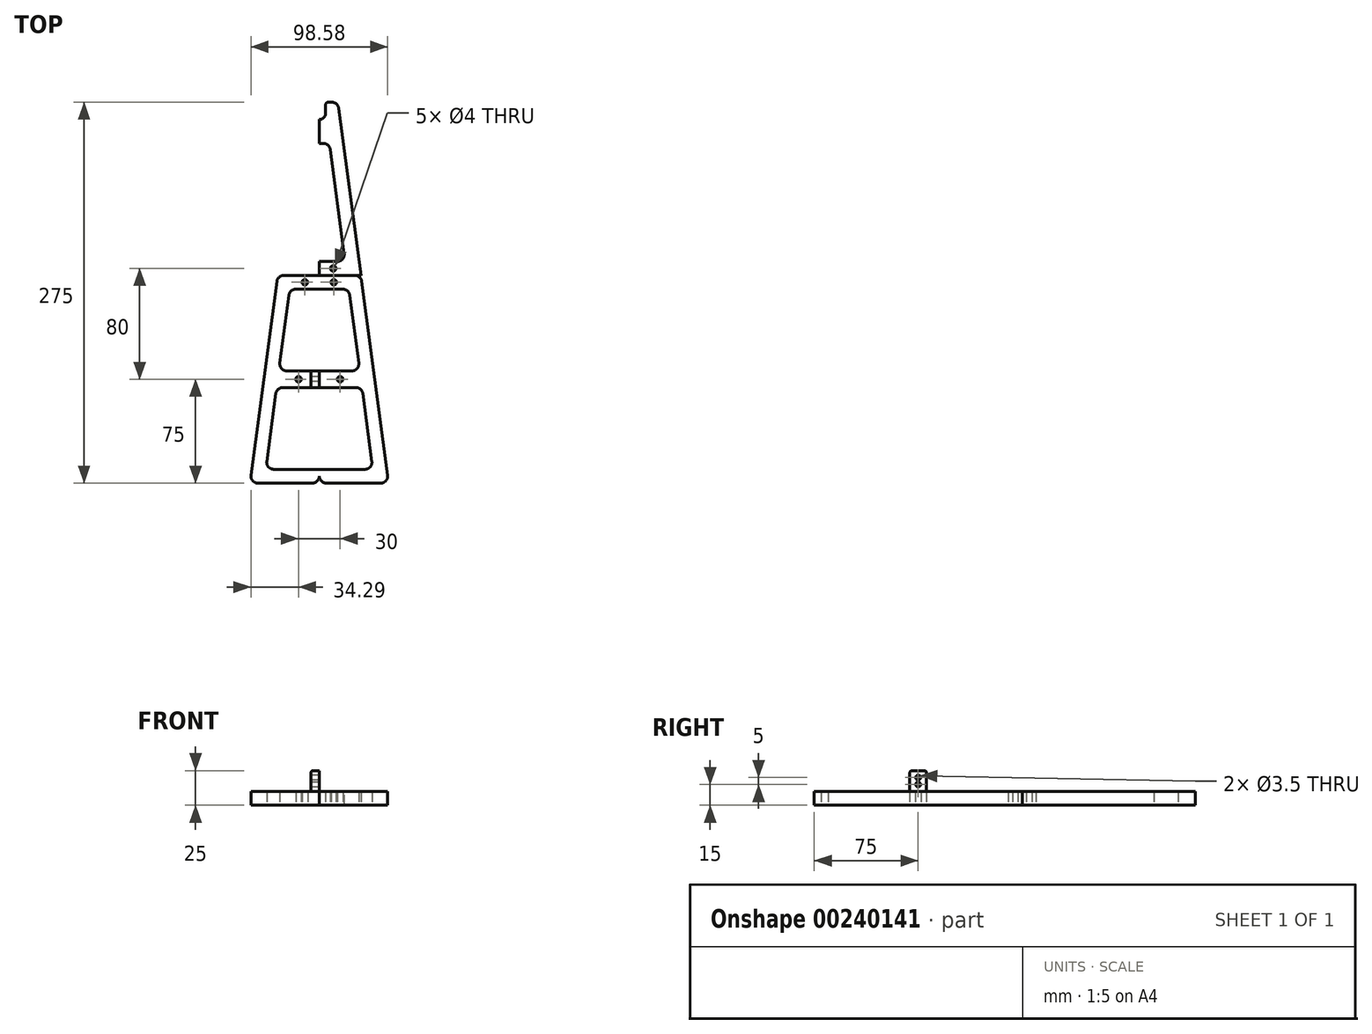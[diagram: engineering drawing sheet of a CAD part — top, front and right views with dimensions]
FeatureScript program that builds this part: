
annotation { "Feature Type Name" : "Feature", "Feature Type Description" : "" }
export const myFeature = defineFeature(function(context is Context, id is Id, definition is map)
    precondition{}
    {
        {
            var Q0;
            Q0=qCreatedBy(makeId("Top.planeOp"),FACE);
            var sketch = newSketch(context, id + "F0", { "sketchPlane" : qUnion([Q0])});
            skLineSegment(sketch, "E0.top", {"start": v(0, 75) * mm, "end": v(-30, 75) * mm});
            skPoint(sketch, "E0.middle", {"position": v(0, 0) * mm});
            skLineSegment(sketch, "E1", {"start": v(-30, 75) * mm, "end": v(-50, -75) * mm});
            skPoint(sketch, "E0.right.end.orphan", {"position": v(-50, 75) * mm});
            skPoint(sketch, "E0.left.end.orphan", {"position": v(50, 75) * mm});
            skLineSegment(sketch, "E2", {"start": v(0, 0) * mm, "end": v(0, 6) * mm});
            skLineSegment(sketch, "E3", {"start": v(-50, -75) * mm, "end": v(-40, -75) * mm});
            skLineSegment(sketch, "E4", {"start": v(-30, 75) * mm, "end": v(-20, 75) * mm});
            skLineSegment(sketch, "E5", {"start": v(0, 75) * mm, "end": v(0, 65) * mm});
            skLineSegment(sketch, "E6", {"start": v(0, 65) * mm, "end": v(-21.33, 65) * mm});
            skLineSegment(sketch, "E7", {"start": v(0, -75) * mm, "end": v(0, -65) * mm});
            skLineSegment(sketch, "E8", {"start": v(0, -65) * mm, "end": v(-38.67, -65) * mm});
            skLineSegment(sketch, "E9", {"start": v(0, 6) * mm, "end": v(-29.2, 6) * mm});
            skLineSegment(sketch, "E10", {"start": v(0, 0) * mm, "end": v(0, -6) * mm});
            skLineSegment(sketch, "E11", {"start": v(0, -6) * mm, "end": v(-30.8, -6) * mm});
            skLineSegment(sketch, "E12.trimOffspring", {"start": v(-30.8, -6) * mm, "end": v(-38.67, -65) * mm});
            skLineSegment(sketch, "E13", {"start": v(-21.33, 65) * mm, "end": v(-29.2, 6) * mm});
            skLineSegment(sketch, "E14.trimOffspring", {"start": v(0, -75) * mm, "end": v(-50, -75) * mm});
            skPoint(sketch, "E0.bottom.start.orphan", {"position": v(50, -75) * mm});
            skCircle(sketch, "E15", {"center": v(-15, 0) * mm, "radius": 2 * mm});
            skLineSegment(sketch, "E16", {"start": v(0, 65) * mm, "end": v(0, 70) * mm});
            skCircle(sketch, "E17", {"center": v(-10.41, 70) * mm, "radius": 2 * mm});
            skSolve(sketch);
        }
        {
            var Q0;
            Q0=qSketchRegion(id+"F0",true);
            extrude(context, id + "F1", {"entities" : qUnion([Q0]), "depth" : 10 * mm});
        }
        {
            var Q0;
            Q0=makeQuery(id+"F1.opExtrude","SWEPT_EDGE",EDGE,{"disambiguationData":[OSD([sQuery(id+"F0.wireOp",EDGE,"E6"),sQuery(id+"F0.wireOp",EDGE,"E13")])]});
            var Q1;
            Q1=makeQuery(id+"F1.opExtrude","SWEPT_EDGE",EDGE,{"disambiguationData":[OSD([sQuery(id+"F0.wireOp",EDGE,"E11"),sQuery(id+"F0.wireOp",EDGE,"E12.trimOffspring")])]});
            var Q2;
            Q2=makeQuery(id+"F1.opExtrude","SWEPT_EDGE",EDGE,{"disambiguationData":[OSD([sQuery(id+"F0.wireOp",EDGE,"E9"),sQuery(id+"F0.wireOp",EDGE,"E13")])]});
            var Q3;
            Q3=makeQuery(id+"F1.opExtrude","SWEPT_EDGE",EDGE,{"disambiguationData":[OSD([sQuery(id+"F0.wireOp",EDGE,"E8"),sQuery(id+"F0.wireOp",EDGE,"E12.trimOffspring")])]});
            var Q4;
            Q4=makeQuery(id+"F1.opExtrude","SWEPT_EDGE",EDGE,{"disambiguationData":[OSD([sQuery(id+"F0.wireOp",EDGE,"E1"),sQuery(id+"F0.wireOp",EDGE,"E14.trimOffspring")])]});
            fillet(context, id + "F2", {"entities" : qUnion([Q0, Q1, Q2, Q3, Q4]), "radius" : 5 * mm, "tangentPropagation" : true, "allowEdgeOverflow" : false});
        }
        {
            var Q0;
            Q0=makeQuery(id+"F1.opExtrude","SWEPT_BODY",BODY,{"disambiguationData":[OSD([sQuery(id+"F0.wireOp",EDGE,"E0.top"),sQuery(id+"F0.wireOp",EDGE,"E1"),sQuery(id+"F0.wireOp",EDGE,"E2"),sQuery(id+"F0.wireOp",EDGE,"E4"),sQuery(id+"F0.wireOp",EDGE,"E5"),sQuery(id+"F0.wireOp",EDGE,"E6"),sQuery(id+"F0.wireOp",EDGE,"E7"),sQuery(id+"F0.wireOp",EDGE,"E8"),sQuery(id+"F0.wireOp",EDGE,"E9"),sQuery(id+"F0.wireOp",EDGE,"E10"),sQuery(id+"F0.wireOp",EDGE,"E11"),sQuery(id+"F0.wireOp",EDGE,"E12.trimOffspring"),sQuery(id+"F0.wireOp",EDGE,"E13"),sQuery(id+"F0.wireOp",EDGE,"E14.trimOffspring"),sQuery(id+"F0.wireOp",EDGE,"E15"),sQuery(id+"F0.wireOp",EDGE,"E16"),sQuery(id+"F0.wireOp",EDGE,"E17")])]});
            var Q1;
            Q1=qCreatedBy(makeId("Right.planeOp"),FACE);
            mirror(context, id + "F3", {"operationType" : NewBodyOperationType.ADD, "entities" : qUnion([Q0]), "mirrorPlane" : qUnion([Q1])});
        }
        {
            var Q0;
            Q0=qCreatedBy(makeId("Top.planeOp"),FACE);
            var sketch = newSketch(context, id + "F4", { "sketchPlane" : qUnion([Q0])});
            skLineSegment(sketch, "E18", {"start": v(0, 0) * mm, "end": v(40, 0) * mm});
            skLineSegment(sketch, "E19", {"start": v(0, 75) * mm, "end": v(30, 75) * mm});
            skLineSegment(sketch, "E20", {"start": v(0, 75) * mm, "end": v(0, 85) * mm});
            skLineSegment(sketch, "E21", {"start": v(4.5, 200) * mm, "end": v(13.33, 200) * mm});
            skLineSegment(sketch, "E22", {"start": v(30, 75) * mm, "end": v(13.33, 200) * mm});
            skArc(sketch, "E23", {"start": v(0, 187.5) * mm, "mid": v(3.18, 188.82) * mm, "end": v(4.5, 192) * mm});
            skLineSegment(sketch, "E24", {"start": v(4.5, 200) * mm, "end": v(4.5, 192) * mm});
            skLineSegment(sketch, "E25", {"start": v(0, 75) * mm, "end": v(0, 80) * mm});
            skCircle(sketch, "E26", {"center": v(10, 80) * mm, "radius": 2 * mm});
            skLineSegment(sketch, "E27", {"start": v(0, 75) * mm, "end": v(10, 75) * mm});
            skLineSegment(sketch, "E28", {"start": v(10, 85) * mm, "end": v(18.67, 85) * mm});
            skLineSegment(sketch, "E29", {"start": v(18.67, 85) * mm, "end": v(10, 150) * mm});
            skLineSegment(sketch, "E30", {"start": v(10, 85) * mm, "end": v(0, 85) * mm});
            skLineSegment(sketch, "E31", {"start": v(18.67, 85) * mm, "end": v(7.31, 170.17) * mm});
            skLineSegment(sketch, "E32", {"start": v(7.31, 170.17) * mm, "end": v(0, 170.17) * mm});
            skLineSegment(sketch, "E33.trimOffspring", {"start": v(0, 170.17) * mm, "end": v(0, 187.5) * mm});
            skSolve(sketch);
        }
        {
            var Q0;
            Q0=qSketchRegion(id+"F4",true);
            extrude(context, id + "F5", {"entities" : qUnion([Q0]), "depth" : 10 * mm});
        }
        {
            var Q0;
            Q0=makeQuery(id+"F5.opExtrude","SWEPT_BODY",BODY,{"disambiguationData":[OSD([sQuery(id+"F4.wireOp",EDGE,"E19"),sQuery(id+"F4.wireOp",EDGE,"E20"),sQuery(id+"F4.wireOp",EDGE,"E21"),sQuery(id+"F4.wireOp",EDGE,"E22"),sQuery(id+"F4.wireOp",EDGE,"E23"),sQuery(id+"F4.wireOp",EDGE,"E24"),sQuery(id+"F4.wireOp",EDGE,"E25"),sQuery(id+"F4.wireOp",EDGE,"E26"),sQuery(id+"F4.wireOp",EDGE,"E27"),sQuery(id+"F4.wireOp",EDGE,"E28"),sQuery(id+"F4.wireOp",EDGE,"E30"),sQuery(id+"F4.wireOp",EDGE,"E31"),sQuery(id+"F4.wireOp",EDGE,"E32"),sQuery(id+"F4.wireOp",EDGE,"E33.trimOffspring")])]});
            var Q1;
            Q1=qCreatedBy(makeId("Right.planeOp"),FACE);
            mirror(context, id + "F6", {"entities" : qUnion([Q0]), "mirrorPlane" : qUnion([Q1])});
        }
        {
            var Q0;
            Q0=makeQuery(id+"F6.opPattern","COPY",EDGE,{"derivedFrom":makeQuery(id+"F5.opExtrude","SWEPT_EDGE",EDGE,{"disambiguationData":[OSD([sQuery(id+"F4.wireOp",EDGE,"E31"),sQuery(id+"F4.wireOp",EDGE,"E32")])]}),"instanceName":"1"});
            var Q1;
            Q1=makeQuery(id+"F5.opExtrude","SWEPT_EDGE",EDGE,{"disambiguationData":[OSD([sQuery(id+"F4.wireOp",EDGE,"E31"),sQuery(id+"F4.wireOp",EDGE,"E32")])]});
            var Q2;
            Q2=makeQuery(id+"F6.opPattern","COPY",EDGE,{"derivedFrom":makeQuery(id+"F5.opExtrude","SWEPT_EDGE",EDGE,{"disambiguationData":[OSD([sQuery(id+"F4.wireOp",EDGE,"E28"),sQuery(id+"F4.wireOp",EDGE,"E31")])]}),"instanceName":"1"});
            var Q3;
            Q3=makeQuery(id+"F5.opExtrude","SWEPT_EDGE",EDGE,{"disambiguationData":[OSD([sQuery(id+"F4.wireOp",EDGE,"E28"),sQuery(id+"F4.wireOp",EDGE,"E31")])]});
            var Q4;
            Q4=makeQuery(id+"F6.opPattern","COPY",EDGE,{"derivedFrom":makeQuery(id+"F5.opExtrude","SWEPT_EDGE",EDGE,{"disambiguationData":[OSD([sQuery(id+"F4.wireOp",EDGE,"E21"),sQuery(id+"F4.wireOp",EDGE,"E22")])]}),"instanceName":"1"});
            var Q5;
            Q5=makeQuery(id+"F5.opExtrude","SWEPT_EDGE",EDGE,{"disambiguationData":[OSD([sQuery(id+"F4.wireOp",EDGE,"E21"),sQuery(id+"F4.wireOp",EDGE,"E22")])]});
            fillet(context, id + "F7", {"entities" : qUnion([Q0, Q1, Q2, Q3, Q4, Q5]), "radius" : 5 * mm, "tangentPropagation" : true, "allowEdgeOverflow" : false});
        }
        {
            var Q0;
            Q0=makeQuery(id+"F5.opExtrude","SWEPT_EDGE",EDGE,{"disambiguationData":[OSD([sQuery(id+"F4.wireOp",EDGE,"E21"),sQuery(id+"F4.wireOp",EDGE,"E24")])]});
            var Q1;
            Q1=makeQuery(id+"F6.opPattern","COPY",EDGE,{"derivedFrom":makeQuery(id+"F5.opExtrude","SWEPT_EDGE",EDGE,{"disambiguationData":[OSD([sQuery(id+"F4.wireOp",EDGE,"E21"),sQuery(id+"F4.wireOp",EDGE,"E24")])]}),"instanceName":"1"});
            fillet(context, id + "F8", {"entities" : qUnion([Q0, Q1]), "radius" : 2 * mm, "tangentPropagation" : true, "allowEdgeOverflow" : false});
        }
        {
            var Q0;
            Q0=qCreatedBy(makeId("Top.planeOp"),FACE);
            var sketch = newSketch(context, id + "F9", { "sketchPlane" : qUnion([Q0])});
            skLineSegment(sketch, "E34", {"start": v(0, 0) * mm, "end": v(0, 6) * mm});
            skLineSegment(sketch, "E35", {"start": v(0, 6) * mm, "end": v(-6, 6) * mm});
            skLineSegment(sketch, "E36", {"start": v(-6, 6) * mm, "end": v(-6, -6) * mm});
            skLineSegment(sketch, "E37", {"start": v(-6, -6) * mm, "end": v(0, -6) * mm});
            skLineSegment(sketch, "E38", {"start": v(0, -6) * mm, "end": v(0, 0) * mm});
            skSolve(sketch);
        }
        {
            var Q0;
            Q0=qSketchRegion(id+"F9",true);
            extrude(context, id + "F10", {"entities" : qUnion([Q0]), "operationType" : NewBodyOperationType.ADD, "depth" : 25 * mm});
        }
        {
            var Q0;
            Q0=makeQuery(id+"F10.opExtrude","SWEPT_EDGE",EDGE,{"disambiguationData":[OSD([sQuery(id+"F9.wireOp",EDGE,"E36"),sQuery(id+"F9.wireOp",EDGE,"E37")])]});
            var Q1;
            Q1=makeQuery(id+"F10.opExtrude","CAP_EDGE",EDGE,{"disambiguationData":[OSD([sQuery(id+"F9.wireOp",EDGE,"E36")])],"isStart":false});
            var Q2;
            Q2=makeQuery(id+"F10.opExtrude","CAP_EDGE",EDGE,{"disambiguationData":[OSD([sQuery(id+"F9.wireOp",EDGE,"E37")])],"isStart":false});
            var Q3;
            Q3=makeQuery(id+"F10.opExtrude","SWEPT_EDGE",EDGE,{"disambiguationData":[OSD([sQuery(id+"F9.wireOp",EDGE,"E35"),sQuery(id+"F9.wireOp",EDGE,"E36")])]});
            var Q4;
            Q4=makeQuery(id+"F10.opExtrude","CAP_EDGE",EDGE,{"disambiguationData":[OSD([sQuery(id+"F9.wireOp",EDGE,"E35")])],"isStart":false});
            fillet(context, id + "F11", {"entities" : qUnion([Q0, Q1, Q2, Q3, Q4]), "radius" : 1.5 * mm, "tangentPropagation" : true, "allowEdgeOverflow" : false});
        }
        {
            var Q0;
            Q0=qCreatedBy(makeId("Right.planeOp"),FACE);
            var sketch = newSketch(context, id + "F12", { "sketchPlane" : qUnion([Q0])});
            skCircle(sketch, "E39", {"center": v(0, 20) * mm, "radius": 1.75 * mm});
            skCircle(sketch, "E40", {"center": v(0, 15) * mm, "radius": 1.75 * mm});
            skSolve(sketch);
        }
        {
            var Q0;
            Q0=qSketchRegion(id+"F12",true);
            extrude(context, id + "F13", {"entities" : qUnion([Q0]), "endBound" : BoundingType.SYMMETRIC, "depth" : 25 * mm});
        }
        {
            var Q0;
            Q0=makeQuery(id+"F13.opExtrude","SWEPT_BODY",BODY,{"disambiguationData":[OSD([sQuery(id+"F12.wireOp",EDGE,"E40")])]});
            var Q1;
            Q1=makeQuery(id+"F13.opExtrude","SWEPT_BODY",BODY,{"disambiguationData":[OSD([sQuery(id+"F12.wireOp",EDGE,"E39")])]});
            var Q2;
            Q2=makeQuery(id+"F1.opExtrude","SWEPT_BODY",BODY,{"disambiguationData":[OSD([sQuery(id+"F0.wireOp",EDGE,"E0.top"),sQuery(id+"F0.wireOp",EDGE,"E1"),sQuery(id+"F0.wireOp",EDGE,"E2"),sQuery(id+"F0.wireOp",EDGE,"E4"),sQuery(id+"F0.wireOp",EDGE,"E5"),sQuery(id+"F0.wireOp",EDGE,"E6"),sQuery(id+"F0.wireOp",EDGE,"E7"),sQuery(id+"F0.wireOp",EDGE,"E8"),sQuery(id+"F0.wireOp",EDGE,"E9"),sQuery(id+"F0.wireOp",EDGE,"E10"),sQuery(id+"F0.wireOp",EDGE,"E11"),sQuery(id+"F0.wireOp",EDGE,"E12.trimOffspring"),sQuery(id+"F0.wireOp",EDGE,"E13"),sQuery(id+"F0.wireOp",EDGE,"E14.trimOffspring"),sQuery(id+"F0.wireOp",EDGE,"E15"),sQuery(id+"F0.wireOp",EDGE,"E16"),sQuery(id+"F0.wireOp",EDGE,"E17")])]});
            booleanBodies(context, id + "F14", {"operationType" : BooleanOperationType.SUBTRACTION, "tools" : qUnion([Q0, Q1]), "targets" : qUnion([Q2])});
        }
        {
            var Q0;
            Q0=qCreatedBy(makeId("Top.planeOp"),FACE);
            var sketch = newSketch(context, id + "F15", { "sketchPlane" : qUnion([Q0])});
            skLineSegment(sketch, "E41.bottom", {"start": v(15, 65) * mm, "end": v(-15, 65) * mm});
            skLineSegment(sketch, "E41.top", {"start": v(15, 85) * mm, "end": v(-15, 85) * mm});
            skLineSegment(sketch, "E41.left", {"start": v(15, 65) * mm, "end": v(15, 85) * mm});
            skLineSegment(sketch, "E41.right", {"start": v(-15, 65) * mm, "end": v(-15, 85) * mm});
            skPoint(sketch, "E41.middle", {"position": v(0, 75) * mm});
            skLineSegment(sketch, "E42", {"start": v(0, 75) * mm, "end": v(0, 85) * mm});
            skLineSegment(sketch, "E43", {"start": v(0, 85) * mm, "end": v(0, 65) * mm});
            skLineSegment(sketch, "E44", {"start": v(0, 65) * mm, "end": v(-6, 65) * mm});
            skLineSegment(sketch, "E45", {"start": v(-6, 65) * mm, "end": v(-6, 85) * mm});
            skLineSegment(sketch, "E46", {"start": v(-6, 85) * mm, "end": v(0, 85) * mm});
            skSolve(sketch);
        }
        {
            var Q0;
            Q0=qSketchRegion(id+"F15",true);
            extrude(context, id + "F16", {"entities" : qUnion([Q0]), "depth" : 10 * mm});
        }
        {
            var Q0;
            Q0=qCreatedBy(makeId("Top.planeOp"),FACE);
            var sketch = newSketch(context, id + "F17", { "sketchPlane" : qUnion([Q0])});
            skLineSegment(sketch, "E47", {"start": v(0, 65) * mm, "end": v(0, 85) * mm});
            skLineSegment(sketch, "E48", {"start": v(0, 85) * mm, "end": v(-6, 85) * mm});
            skLineSegment(sketch, "E49", {"start": v(-6, 85) * mm, "end": v(-6, 65) * mm});
            skLineSegment(sketch, "E50", {"start": v(-6, 65) * mm, "end": v(0, 65) * mm});
            skSolve(sketch);
        }
        {
            var Q0;
            Q0=qSketchRegion(id+"F17",true);
            extrude(context, id + "F18", {"entities" : qUnion([Q0]), "depth" : 25 * mm});
        }
        {
            var Q0;
            Q0=makeQuery(id+"F16.opExtrude","SWEPT_BODY",BODY,{"disambiguationData":[OSD([sQuery(id+"F15.wireOp",EDGE,"E41.bottom"),sQuery(id+"F15.wireOp",EDGE,"E41.top"),sQuery(id+"F15.wireOp",EDGE,"E41.left"),sQuery(id+"F15.wireOp",EDGE,"E41.right"),sQuery(id+"F15.wireOp",EDGE,"E44"),sQuery(id+"F15.wireOp",EDGE,"E46")])]});
            var Q1;
            Q1=makeQuery(id+"F18.opExtrude","SWEPT_BODY",BODY,{"disambiguationData":[OSD([sQuery(id+"F17.wireOp",EDGE,"E47"),sQuery(id+"F17.wireOp",EDGE,"E48"),sQuery(id+"F17.wireOp",EDGE,"E49"),sQuery(id+"F17.wireOp",EDGE,"E50")])]});
            booleanBodies(context, id + "F19", {"operationType" : BooleanOperationType.UNION, "tools" : qUnion([Q0, Q1])});
        }
        {
            var Q0;
            Q0=makeQuery(id+"F16.opExtrude","SWEPT_BODY",BODY,{"disambiguationData":[OSD([sQuery(id+"F15.wireOp",EDGE,"E41.bottom"),sQuery(id+"F15.wireOp",EDGE,"E41.top"),sQuery(id+"F15.wireOp",EDGE,"E41.left"),sQuery(id+"F15.wireOp",EDGE,"E41.right"),sQuery(id+"F15.wireOp",EDGE,"E44"),sQuery(id+"F15.wireOp",EDGE,"E46")])]});
            transform(context, id + "F20", {"entities" : qUnion([Q0]), "transformType" : TransformType.TRANSLATION_3D, "dx" : 0 * mm, "dy" : 0 * mm, "dz" : 10 * mm, "makeCopy" : false});
        }
        {
            var Q0;
            Q0=qCreatedBy(makeId("Top.planeOp"),FACE);
            var sketch = newSketch(context, id + "F21", { "sketchPlane" : qUnion([Q0])});
            skCircle(sketch, "E51", {"center": v(-10, 80) * mm, "radius": 2 * mm});
            skCircle(sketch, "E52", {"center": v(10, 80) * mm, "radius": 2 * mm});
            skCircle(sketch, "E53", {"center": v(-10.4, 70) * mm, "radius": 2 * mm});
            skCircle(sketch, "E54", {"center": v(10.4, 70) * mm, "radius": 2 * mm});
            skSolve(sketch);
        }
        {
            var Q0;
            Q0=qSketchRegion(id+"F21",true);
            extrude(context, id + "F22", {"entities" : qUnion([Q0]), "depth" : 30 * mm});
        }
        {
            var Q0;
            Q0=makeQuery(id+"F22.opExtrude","SWEPT_BODY",BODY,{"disambiguationData":[OSD([sQuery(id+"F21.wireOp",EDGE,"E54")])]});
            var Q1;
            Q1=makeQuery(id+"F22.opExtrude","SWEPT_BODY",BODY,{"disambiguationData":[OSD([sQuery(id+"F21.wireOp",EDGE,"E53")])]});
            var Q2;
            Q2=makeQuery(id+"F22.opExtrude","SWEPT_BODY",BODY,{"disambiguationData":[OSD([sQuery(id+"F21.wireOp",EDGE,"E52")])]});
            var Q3;
            Q3=makeQuery(id+"F22.opExtrude","SWEPT_BODY",BODY,{"disambiguationData":[OSD([sQuery(id+"F21.wireOp",EDGE,"E51")])]});
            var Q4;
            Q4=makeQuery(id+"F16.opExtrude","SWEPT_BODY",BODY,{"disambiguationData":[OSD([sQuery(id+"F15.wireOp",EDGE,"E41.bottom"),sQuery(id+"F15.wireOp",EDGE,"E41.top"),sQuery(id+"F15.wireOp",EDGE,"E41.left"),sQuery(id+"F15.wireOp",EDGE,"E41.right"),sQuery(id+"F15.wireOp",EDGE,"E44"),sQuery(id+"F15.wireOp",EDGE,"E46")])]});
            booleanBodies(context, id + "F23", {"operationType" : BooleanOperationType.SUBTRACTION, "tools" : qUnion([Q0, Q1, Q2, Q3]), "targets" : qUnion([Q4])});
        }
        {
            var Q0;
            Q0=qCreatedBy(makeId("Right.planeOp"),FACE);
            var sketch = newSketch(context, id + "F24", { "sketchPlane" : qUnion([Q0])});
            skCircle(sketch, "E55", {"center": v(80, 27.23) * mm, "radius": 2 * mm});
            skCircle(sketch, "E56", {"center": v(70, 27.23) * mm, "radius": 2 * mm});
            skSolve(sketch);
        }
        {
            var Q0;
            Q0=qSketchRegion(id+"F24",true);
            extrude(context, id + "F25", {"entities" : qUnion([Q0]), "endBound" : BoundingType.SYMMETRIC, "depth" : 25 * mm});
        }
        {
            var Q0;
            Q0=makeQuery(id+"F25.opExtrude","SWEPT_BODY",BODY,{"disambiguationData":[OSD([sQuery(id+"F24.wireOp",EDGE,"E56")])]});
            var Q1;
            Q1=makeQuery(id+"F25.opExtrude","SWEPT_BODY",BODY,{"disambiguationData":[OSD([sQuery(id+"F24.wireOp",EDGE,"E55")])]});
            var Q2;
            Q2=makeQuery(id+"F16.opExtrude","SWEPT_BODY",BODY,{"disambiguationData":[OSD([sQuery(id+"F15.wireOp",EDGE,"E41.bottom"),sQuery(id+"F15.wireOp",EDGE,"E41.top"),sQuery(id+"F15.wireOp",EDGE,"E41.left"),sQuery(id+"F15.wireOp",EDGE,"E41.right"),sQuery(id+"F15.wireOp",EDGE,"E44"),sQuery(id+"F15.wireOp",EDGE,"E46")])]});
            booleanBodies(context, id + "F26", {"operationType" : BooleanOperationType.SUBTRACTION, "tools" : qUnion([Q0, Q1]), "targets" : qUnion([Q2])});
        }
        {
            var Q0;
            Q0=makeQuery(id+"F18.opExtrude","SWEPT_EDGE",EDGE,{"disambiguationData":[OSD([sQuery(id+"F17.wireOp",EDGE,"E49"),sQuery(id+"F17.wireOp",EDGE,"E50")])]});
            var Q1;
            Q1=makeQuery(id+"F18.opExtrude","CAP_EDGE",EDGE,{"disambiguationData":[OSD([sQuery(id+"F17.wireOp",EDGE,"E50")])],"isStart":false});
            var Q2;
            {var subQ0=sQuery(id+"F15.wireOp",EDGE,"E44");var subQ1=sQuery(id+"F15.wireOp",EDGE,"E41.bottom");var subQ2=sQuery(id+"F15.wireOp",EDGE,"E41.right");Q2=makeQuery(id+"F19.opBoolean","SPLIT",EDGE,{"disambiguationData":[TD([makeQuery(id+"F16.opExtrude","SWEPT_FACE",FACE,{"disambiguationData":[OSD([subQ2])]})])],"derivedFrom":makeQuery(id+"F16.opExtrude","CAP_EDGE",EDGE,{"disambiguationData":[OSD([subQ1,subQ0])],"isStart":false})});}
            var Q3;
            Q3=makeQuery(id+"F16.opExtrude","SWEPT_EDGE",EDGE,{"disambiguationData":[OSD([sQuery(id+"F15.wireOp",EDGE,"E41.bottom"),sQuery(id+"F15.wireOp",EDGE,"E41.right")])]});
            var Q4;
            {var subQ0=sQuery(id+"F15.wireOp",EDGE,"E41.left");var subQ1=sQuery(id+"F15.wireOp",EDGE,"E44");var subQ2=sQuery(id+"F15.wireOp",EDGE,"E41.bottom");Q4=makeQuery(id+"F19.opBoolean","SPLIT",EDGE,{"disambiguationData":[TD([makeQuery(id+"F16.opExtrude","SWEPT_FACE",FACE,{"disambiguationData":[OSD([subQ0])]})])],"derivedFrom":makeQuery(id+"F16.opExtrude","CAP_EDGE",EDGE,{"disambiguationData":[OSD([subQ2,subQ1])],"isStart":false})});}
            var Q5;
            Q5=makeQuery(id+"F16.opExtrude","SWEPT_EDGE",EDGE,{"disambiguationData":[OSD([sQuery(id+"F15.wireOp",EDGE,"E41.bottom"),sQuery(id+"F15.wireOp",EDGE,"E41.left")])]});
            var Q6;
            Q6=makeQuery(id+"F16.opExtrude","CAP_EDGE",EDGE,{"disambiguationData":[OSD([sQuery(id+"F15.wireOp",EDGE,"E41.left")])],"isStart":false});
            var Q7;
            Q7=makeQuery(id+"F16.opExtrude","CAP_EDGE",EDGE,{"disambiguationData":[OSD([sQuery(id+"F15.wireOp",EDGE,"E41.right")])],"isStart":false});
            var Q8;
            Q8=makeQuery(id+"F18.opExtrude","CAP_EDGE",EDGE,{"disambiguationData":[OSD([sQuery(id+"F17.wireOp",EDGE,"E49")])],"isStart":false});
            var Q9;
            {var subQ0=sQuery(id+"F15.wireOp",EDGE,"E41.right");var subQ1=sQuery(id+"F15.wireOp",EDGE,"E46");var subQ2=sQuery(id+"F15.wireOp",EDGE,"E41.top");Q9=makeQuery(id+"F19.opBoolean","SPLIT",EDGE,{"disambiguationData":[TD([makeQuery(id+"F16.opExtrude","SWEPT_FACE",FACE,{"disambiguationData":[OSD([subQ0])]})])],"derivedFrom":makeQuery(id+"F16.opExtrude","CAP_EDGE",EDGE,{"disambiguationData":[OSD([subQ2,subQ1])],"isStart":false})});}
            var Q10;
            Q10=makeQuery(id+"F16.opExtrude","SWEPT_EDGE",EDGE,{"disambiguationData":[OSD([sQuery(id+"F15.wireOp",EDGE,"E41.top"),sQuery(id+"F15.wireOp",EDGE,"E41.right")])]});
            var Q11;
            Q11=makeQuery(id+"F18.opExtrude","SWEPT_EDGE",EDGE,{"disambiguationData":[OSD([sQuery(id+"F17.wireOp",EDGE,"E48"),sQuery(id+"F17.wireOp",EDGE,"E49")])]});
            var Q12;
            Q12=makeQuery(id+"F18.opExtrude","CAP_EDGE",EDGE,{"disambiguationData":[OSD([sQuery(id+"F17.wireOp",EDGE,"E48")])],"isStart":false});
            var Q13;
            {var subQ0=sQuery(id+"F15.wireOp",EDGE,"E41.left");var subQ1=sQuery(id+"F15.wireOp",EDGE,"E46");var subQ2=sQuery(id+"F15.wireOp",EDGE,"E41.top");Q13=makeQuery(id+"F19.opBoolean","SPLIT",EDGE,{"disambiguationData":[TD([makeQuery(id+"F16.opExtrude","SWEPT_FACE",FACE,{"disambiguationData":[OSD([subQ0])]})])],"derivedFrom":makeQuery(id+"F16.opExtrude","CAP_EDGE",EDGE,{"disambiguationData":[OSD([subQ2,subQ1])],"isStart":false})});}
            var Q14;
            Q14=makeQuery(id+"F16.opExtrude","SWEPT_EDGE",EDGE,{"disambiguationData":[OSD([sQuery(id+"F15.wireOp",EDGE,"E41.top"),sQuery(id+"F15.wireOp",EDGE,"E41.left")])]});
            fillet(context, id + "F27", {"entities" : qUnion([Q0, Q1, Q2, Q3, Q4, Q5, Q6, Q7, Q8, Q9, Q10, Q11, Q12, Q13, Q14]), "radius" : 2 * mm, "tangentPropagation" : true, "allowEdgeOverflow" : false});
        }
        {
            var Q0;
            Q0=qCreatedBy(makeId("Right.planeOp"),FACE);
            var sketch = newSketch(context, id + "F28", { "sketchPlane" : qUnion([Q0])});
            skLineSegment(sketch, "E57", {"start": v(0, 0) * mm, "end": v(0, 10) * mm});
            skLineSegment(sketch, "E58", {"start": v(0, 10) * mm, "end": v(6, 10) * mm});
            skLineSegment(sketch, "E59", {"start": v(6, 10) * mm, "end": v(6, 25) * mm});
            skLineSegment(sketch, "E60", {"start": v(-6, 25) * mm, "end": v(-6, 10) * mm});
            skLineSegment(sketch, "E61", {"start": v(-6, 10) * mm, "end": v(0, 10) * mm});
            skLineSegment(sketch, "E62", {"start": v(75, 10) * mm, "end": v(75, 20) * mm});
            skLineSegment(sketch, "E63", {"start": v(75, 20) * mm, "end": v(85, 20) * mm});
            skLineSegment(sketch, "E64", {"start": v(85, 20) * mm, "end": v(85, 35) * mm});
            skLineSegment(sketch, "E65", {"start": v(65, 35) * mm, "end": v(65, 20) * mm});
            skLineSegment(sketch, "E66", {"start": v(65, 20) * mm, "end": v(75, 20) * mm});
            skLineSegment(sketch, "E67", {"start": v(-6, 10) * mm, "end": v(-6, 25) * mm});
            skLineSegment(sketch, "E68", {"start": v(75, 120) * mm, "end": v(85, 120) * mm});
            skLineSegment(sketch, "E69", {"start": v(85, 35) * mm, "end": v(85, 120) * mm});
            skLineSegment(sketch, "E70", {"start": v(85, 120) * mm, "end": v(75, 120) * mm});
            skLineSegment(sketch, "E71", {"start": v(6, 25) * mm, "end": v(65, 35) * mm});
            skLineSegment(sketch, "E72", {"start": v(-6, 25) * mm, "end": v(75, 120) * mm});
            skLineSegment(sketch, "E73", {"start": v(23.92, 44.68) * mm, "end": v(75, 104.59) * mm});
            skLineSegment(sketch, "E74", {"start": v(23.92, 44.68) * mm, "end": v(17.44, 37.08) * mm});
            skLineSegment(sketch, "E75", {"start": v(75, 45) * mm, "end": v(64.16, 45) * mm});
            skLineSegment(sketch, "E76", {"start": v(51.92, 42.93) * mm, "end": v(17.44, 37.08) * mm});
            skLineSegment(sketch, "E77", {"start": v(51.92, 42.93) * mm, "end": v(64.16, 45) * mm});
            skPoint(sketch, "E78.orphan", {"position": v(75, 35) * mm});
            skPoint(sketch, "E79.start.orphan", {"position": v(75, 110) * mm});
            skLineSegment(sketch, "E80", {"start": v(75, 104.59) * mm, "end": v(75, 45) * mm});
            skCircle(sketch, "E81", {"center": v(80, 110) * mm, "radius": 2 * mm});
            skCircle(sketch, "E82", {"center": v(80, 95) * mm, "radius": 2 * mm});
            skPoint(sketch, "E83.end.orphan", {"position": v(80, 120) * mm});
            skSolve(sketch);
        }
        {
            var Q0;
            Q0=qSketchRegion(id+"F28",true);
            extrude(context, id + "F29", {"entities" : qUnion([Q0]), "depth" : 8 * mm});
        }
        {
            var Q0;
            Q0=makeQuery(id+"F29.opExtrude","SWEPT_EDGE",EDGE,{"disambiguationData":[OSD([sQuery(id+"F28.wireOp",EDGE,"E73"),sQuery(id+"F28.wireOp",EDGE,"E80")])]});
            var Q1;
            Q1=makeQuery(id+"F29.opExtrude","SWEPT_EDGE",EDGE,{"disambiguationData":[OSD([sQuery(id+"F28.wireOp",EDGE,"E75"),sQuery(id+"F28.wireOp",EDGE,"E80")])]});
            var Q2;
            Q2=makeQuery(id+"F29.opExtrude","SWEPT_EDGE",EDGE,{"disambiguationData":[OSD([sQuery(id+"F28.wireOp",EDGE,"E74"),sQuery(id+"F28.wireOp",EDGE,"E76")])]});
            var Q3;
            Q3=makeQuery(id+"F29.opExtrude","SWEPT_EDGE",EDGE,{"disambiguationData":[OSD([sQuery(id+"F28.wireOp",EDGE,"E65"),sQuery(id+"F28.wireOp",EDGE,"E71")])]});
            var Q4;
            Q4=makeQuery(id+"F29.opExtrude","SWEPT_EDGE",EDGE,{"disambiguationData":[OSD([sQuery(id+"F28.wireOp",EDGE,"E59"),sQuery(id+"F28.wireOp",EDGE,"E71")])]});
            var Q5;
            Q5=makeQuery(id+"F29.opExtrude","SWEPT_EDGE",EDGE,{"disambiguationData":[OSD([sQuery(id+"F28.wireOp",EDGE,"E67"),sQuery(id+"F28.wireOp",EDGE,"E72")])]});
            fillet(context, id + "F30", {"entities" : qUnion([Q0, Q1, Q2, Q3, Q4, Q5]), "radius" : 2 * mm, "tangentPropagation" : true, "allowEdgeOverflow" : false});
        }
        {
            var Q0;
            Q0=makeQuery(id+"F29.opExtrude","CAP_EDGE",EDGE,{"disambiguationData":[OSD([sQuery(id+"F28.wireOp",EDGE,"E73"),sQuery(id+"F28.wireOp",EDGE,"E74")])],"isStart":false});
            var Q1;
            Q1=makeQuery(id+"F29.opExtrude","CAP_EDGE",EDGE,{"disambiguationData":[OSD([sQuery(id+"F28.wireOp",EDGE,"E72")])],"isStart":false});
            var Q2;
            Q2=makeQuery(id+"F29.opExtrude","CAP_EDGE",EDGE,{"disambiguationData":[OSD([sQuery(id+"F28.wireOp",EDGE,"E71")])],"isStart":false});
            var Q3;
            Q3=makeQuery(id+"F29.opExtrude","CAP_EDGE",EDGE,{"disambiguationData":[OSD([sQuery(id+"F28.wireOp",EDGE,"E64"),sQuery(id+"F28.wireOp",EDGE,"E69")])],"isStart":false});
            fillet(context, id + "F31", {"entities" : qUnion([Q0, Q1, Q2, Q3]), "radius" : 2 * mm, "tangentPropagation" : true, "allowEdgeOverflow" : false});
        }
        {
            var Q0;
            Q0=qCreatedBy(makeId("Right.planeOp"),FACE);
            var sketch = newSketch(context, id + "F32", { "sketchPlane" : qUnion([Q0])});
            skCircle(sketch, "E84", {"center": v(0, 20) * mm, "radius": 1.75 * mm});
            skCircle(sketch, "E85", {"center": v(0, 15) * mm, "radius": 1.75 * mm});
            skCircle(sketch, "E86", {"center": v(70, 27.25) * mm, "radius": 2 * mm});
            skCircle(sketch, "E87", {"center": v(80, 27.25) * mm, "radius": 2 * mm});
            skSolve(sketch);
        }
        {
            var Q0;
            Q0=qSketchRegion(id+"F32",true);
            extrude(context, id + "F33", {"entities" : qUnion([Q0]), "depth" : 25 * mm});
        }
        {
            var Q0;
            Q0=makeQuery(id+"F33.opExtrude","SWEPT_BODY",BODY,{"disambiguationData":[OSD([sQuery(id+"F32.wireOp",EDGE,"E87")])]});
            var Q1;
            Q1=makeQuery(id+"F33.opExtrude","SWEPT_BODY",BODY,{"disambiguationData":[OSD([sQuery(id+"F32.wireOp",EDGE,"E86")])]});
            var Q2;
            Q2=makeQuery(id+"F33.opExtrude","SWEPT_BODY",BODY,{"disambiguationData":[OSD([sQuery(id+"F32.wireOp",EDGE,"E85")])]});
            var Q3;
            Q3=makeQuery(id+"F33.opExtrude","SWEPT_BODY",BODY,{"disambiguationData":[OSD([sQuery(id+"F32.wireOp",EDGE,"E84")])]});
            var Q4;
            Q4=makeQuery(id+"F29.opExtrude","SWEPT_BODY",BODY,{"disambiguationData":[OSD([sQuery(id+"F28.wireOp",EDGE,"E59"),sQuery(id+"F28.wireOp",EDGE,"E61"),sQuery(id+"F28.wireOp",EDGE,"E58"),sQuery(id+"F28.wireOp",EDGE,"E63"),sQuery(id+"F28.wireOp",EDGE,"E64"),sQuery(id+"F28.wireOp",EDGE,"E65"),sQuery(id+"F28.wireOp",EDGE,"E66"),sQuery(id+"F28.wireOp",EDGE,"E67"),sQuery(id+"F28.wireOp",EDGE,"E69"),sQuery(id+"F28.wireOp",EDGE,"E70"),sQuery(id+"F28.wireOp",EDGE,"E71"),sQuery(id+"F28.wireOp",EDGE,"E72"),sQuery(id+"F28.wireOp",EDGE,"E73"),sQuery(id+"F28.wireOp",EDGE,"E74"),sQuery(id+"F28.wireOp",EDGE,"E75"),sQuery(id+"F28.wireOp",EDGE,"E76"),sQuery(id+"F28.wireOp",EDGE,"E77"),sQuery(id+"F28.wireOp",EDGE,"E80"),sQuery(id+"F28.wireOp",EDGE,"E81"),sQuery(id+"F28.wireOp",EDGE,"E82")])]});
            booleanBodies(context, id + "F34", {"operationType" : BooleanOperationType.SUBTRACTION, "tools" : qUnion([Q0, Q1, Q2, Q3]), "targets" : qUnion([Q4])});
        }
        {
            var Q0;
            Q0=makeQuery(id+"F6.opPattern","COPY",BODY,{"derivedFrom":makeQuery(id+"F5.opExtrude","SWEPT_BODY",BODY,{"disambiguationData":[OSD([sQuery(id+"F4.wireOp",EDGE,"E19"),sQuery(id+"F4.wireOp",EDGE,"E20"),sQuery(id+"F4.wireOp",EDGE,"E21"),sQuery(id+"F4.wireOp",EDGE,"E22"),sQuery(id+"F4.wireOp",EDGE,"E23"),sQuery(id+"F4.wireOp",EDGE,"E24"),sQuery(id+"F4.wireOp",EDGE,"E25"),sQuery(id+"F4.wireOp",EDGE,"E26"),sQuery(id+"F4.wireOp",EDGE,"E27"),sQuery(id+"F4.wireOp",EDGE,"E28"),sQuery(id+"F4.wireOp",EDGE,"E30"),sQuery(id+"F4.wireOp",EDGE,"E31"),sQuery(id+"F4.wireOp",EDGE,"E32"),sQuery(id+"F4.wireOp",EDGE,"E33.trimOffspring")])]}),"instanceName":"1"});
            var Q1;
            Q1=makeQuery(id+"F16.opExtrude","SWEPT_BODY",BODY,{"disambiguationData":[OSD([sQuery(id+"F15.wireOp",EDGE,"E41.bottom"),sQuery(id+"F15.wireOp",EDGE,"E41.top"),sQuery(id+"F15.wireOp",EDGE,"E41.left"),sQuery(id+"F15.wireOp",EDGE,"E41.right"),sQuery(id+"F15.wireOp",EDGE,"E44"),sQuery(id+"F15.wireOp",EDGE,"E46")])]});
            var Q2;
            Q2=makeQuery(id+"F29.opExtrude","SWEPT_BODY",BODY,{"disambiguationData":[OSD([sQuery(id+"F28.wireOp",EDGE,"E59"),sQuery(id+"F28.wireOp",EDGE,"E61"),sQuery(id+"F28.wireOp",EDGE,"E58"),sQuery(id+"F28.wireOp",EDGE,"E63"),sQuery(id+"F28.wireOp",EDGE,"E64"),sQuery(id+"F28.wireOp",EDGE,"E65"),sQuery(id+"F28.wireOp",EDGE,"E66"),sQuery(id+"F28.wireOp",EDGE,"E67"),sQuery(id+"F28.wireOp",EDGE,"E69"),sQuery(id+"F28.wireOp",EDGE,"E70"),sQuery(id+"F28.wireOp",EDGE,"E71"),sQuery(id+"F28.wireOp",EDGE,"E72"),sQuery(id+"F28.wireOp",EDGE,"E73"),sQuery(id+"F28.wireOp",EDGE,"E74"),sQuery(id+"F28.wireOp",EDGE,"E75"),sQuery(id+"F28.wireOp",EDGE,"E76"),sQuery(id+"F28.wireOp",EDGE,"E77"),sQuery(id+"F28.wireOp",EDGE,"E80"),sQuery(id+"F28.wireOp",EDGE,"E81"),sQuery(id+"F28.wireOp",EDGE,"E82")])]});
            deleteBodies(context, id + "F35", {"entities" : qUnion([Q0, Q1, Q2])});
        }
    });
